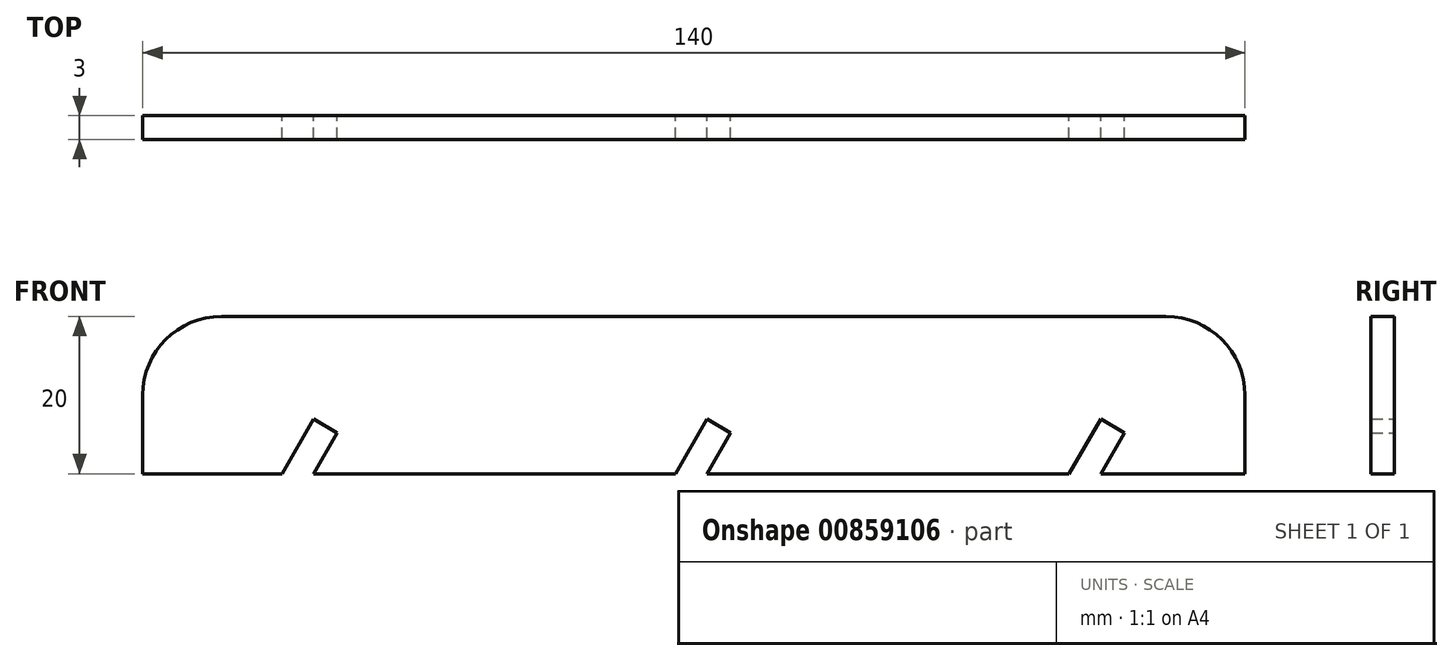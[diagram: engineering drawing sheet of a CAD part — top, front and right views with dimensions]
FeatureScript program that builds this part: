
annotation { "Feature Type Name" : "Feature", "Feature Type Description" : "" }
export const myFeature = defineFeature(function(context is Context, id is Id, definition is map)
    precondition{}
    {
        {
            var Q0;
            Q0=qCreatedBy(makeId("Front.planeOp"),FACE);
            var sketch = newSketch(context, id + "F0", { "sketchPlane" : qUnion([Q0])});
            skLineSegment(sketch, "E0.top", {"start": v(70, -10) * mm, "end": v(-70, -10) * mm});
            skPoint(sketch, "E0.middle", {"position": v(0, 0) * mm});
            skLineSegment(sketch, "E1", {"start": v(-70, -10) * mm, "end": v(-70, 0) * mm});
            skLineSegment(sketch, "E2", {"start": v(70, -10) * mm, "end": v(70, 0) * mm});
            skLineSegment(sketch, "E3", {"start": v(60, 10) * mm, "end": v(-60, 10) * mm});
            skArc(sketch, "E4", {"start": v(-70, 0) * mm, "mid": v(-67.07, 7.07) * mm, "end": v(-60, 10) * mm});
            skArc(sketch, "E5", {"start": v(70, 0) * mm, "mid": v(67.07, 7.07) * mm, "end": v(60, 10) * mm});
            skLineSegment(sketch, "E6", {"start": v(-70, -10) * mm, "end": v(-50.31, -10) * mm});
            skLineSegment(sketch, "E7", {"start": v(-50.31, -10) * mm, "end": v(0, -10) * mm});
            skLineSegment(sketch, "E8", {"start": v(0, -10) * mm, "end": v(50, -10) * mm});
            skLineSegment(sketch, "E9", {"start": v(-50.31, -10) * mm, "end": v(-52.31, -10) * mm});
            skLineSegment(sketch, "E10", {"start": v(-52.31, -10) * mm, "end": v(-48.31, -10) * mm});
            skLineSegment(sketch, "E11", {"start": v(-48.31, -10) * mm, "end": v(-45.31, -4.8) * mm});
            skLineSegment(sketch, "E12", {"start": v(-48.3, -3.06) * mm, "end": v(-52.31, -10) * mm});
            skLineSegment(sketch, "E13", {"start": v(-48.3, -3.06) * mm, "end": v(-45.31, -4.8) * mm});
            skLineSegment(sketch, "E14.1.0.0", {"start": v(1.7, -3.06) * mm, "end": v(-2.31, -10) * mm});
            skLineSegment(sketch, "E14.1.0.1", {"start": v(-2.31, -10) * mm, "end": v(1.69, -10) * mm});
            skLineSegment(sketch, "E14.1.0.2", {"start": v(1.69, -10) * mm, "end": v(4.69, -4.8) * mm});
            skLineSegment(sketch, "E14.1.0.3", {"start": v(1.7, -3.06) * mm, "end": v(4.69, -4.8) * mm});
            skLineSegment(sketch, "E14.2.0.0", {"start": v(51.7, -3.06) * mm, "end": v(47.69, -10) * mm});
            skLineSegment(sketch, "E14.2.0.1", {"start": v(47.69, -10) * mm, "end": v(51.69, -10) * mm});
            skLineSegment(sketch, "E14.2.0.2", {"start": v(51.69, -10) * mm, "end": v(54.69, -4.8) * mm});
            skLineSegment(sketch, "E14.2.0.3", {"start": v(51.7, -3.06) * mm, "end": v(54.69, -4.8) * mm});
            skLineSegment(sketch, "E14.direction1", {"start": v(-52.31, -10) * mm, "end": v(-2.31, -10) * mm, "construction": true});
            skSolve(sketch);
        }
        {
            var Q0;
            Q0=makeQuery(id+"F0.imprint","IMPRINT",FACE,{"disambiguationData":[TD([[makeQuery(id+"F0.imprint","IMPRINT",EDGE,{"derivedFrom":sQuery(id+"F0.wireOp",EDGE,"E0.top")}),-1.0]])]});
            extrude(context, id + "F1", {"entities" : qUnion([Q0]), "depth" : 3 * mm, "offsetDistance" : 25 * mm});
        }
    });
